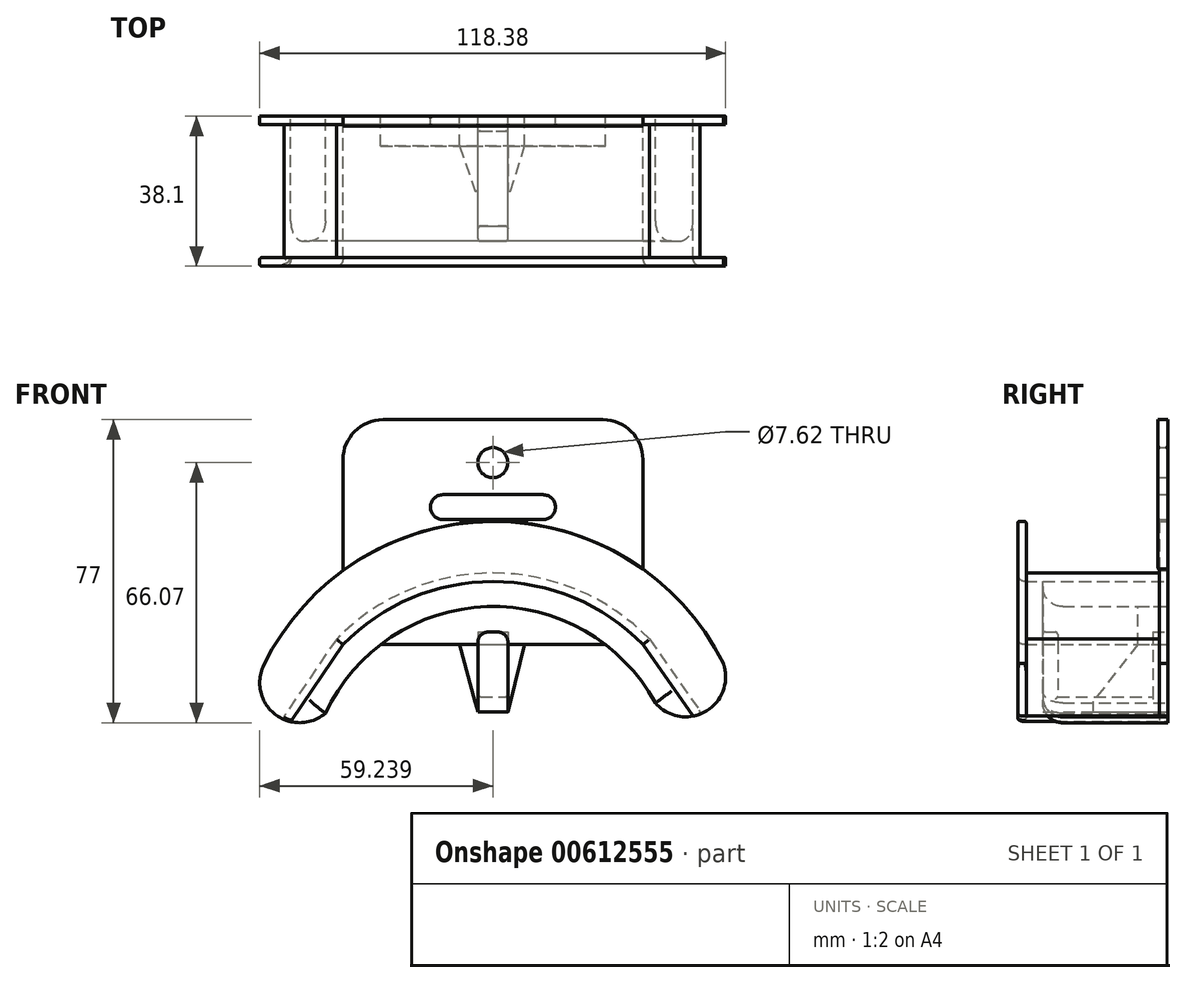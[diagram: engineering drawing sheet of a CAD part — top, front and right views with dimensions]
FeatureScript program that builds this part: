
annotation { "Feature Type Name" : "Feature", "Feature Type Description" : "" }
export const myFeature = defineFeature(function(context is Context, id is Id, definition is map)
    precondition{}
    {
        {
            var Q0;
            Q0=qCreatedBy(makeId("Front.planeOp"),FACE);
            var sketch = newSketch(context, id + "F0", { "sketchPlane" : qUnion([Q0])});
            skLineSegment(sketch, "E0.bottom", {"start": v(-38.1, 57.15) * mm, "end": v(38.1, 57.15) * mm});
            skLineSegment(sketch, "E0.top", {"start": v(-38.1, 0) * mm, "end": v(38.1, 0) * mm});
            skLineSegment(sketch, "E0.left", {"start": v(-38.1, 57.15) * mm, "end": v(-38.1, 0) * mm});
            skLineSegment(sketch, "E0.right", {"start": v(38.1, 57.15) * mm, "end": v(38.1, 0) * mm});
            skArc(sketch, "E1", {"start": v(38.1, 0) * mm, "mid": v(0, 16.02) * mm, "end": v(-38.1, 0) * mm});
            skArc(sketch, "E2.0", {"start": v(41.24, -14.8) * mm, "mid": v(-1.5, 9.64) * mm, "end": v(-42.58, -17.48) * mm});
            skArc(sketch, "E3", {"start": v(-58.24, -5.23) * mm, "mid": v(-55.37, -17.7) * mm, "end": v(-42.58, -17.48) * mm});
            skArc(sketch, "E4", {"start": v(41.24, -14.8) * mm, "mid": v(54.07, -16.97) * mm, "end": v(58.5, -4.73) * mm});
            skLineSegment(sketch, "E5.bottom", {"start": v(-8.48, 0) * mm, "end": v(8.03, 0) * mm});
            skLineSegment(sketch, "E5.right", {"start": v(8.35, 0) * mm, "end": v(8.03, 0) * mm});
            skLineSegment(sketch, "E6", {"start": v(-8.48, 0) * mm, "end": v(-3.83, -17.13) * mm});
            skLineSegment(sketch, "E7", {"start": v(-3.83, -17.13) * mm, "end": v(3.81, -17.13) * mm});
            skLineSegment(sketch, "E8", {"start": v(3.81, -17.13) * mm, "end": v(8.03, 0) * mm});
            skLineSegment(sketch, "E9.bottom", {"start": v(-3.81, 3.2) * mm, "end": v(3.8, 3.2) * mm});
            skLineSegment(sketch, "E9.top", {"start": v(-3.8, -17.13) * mm, "end": v(3.81, -17.13) * mm});
            skLineSegment(sketch, "E9.left", {"start": v(-3.81, 3.2) * mm, "end": v(-3.8, -17.13) * mm});
            skLineSegment(sketch, "E9.right", {"start": v(3.8, 3.2) * mm, "end": v(3.81, -17.13) * mm});
            skLineSegment(sketch, "E10.bottom", {"start": v(-12.7, 38.09) * mm, "end": v(12.7, 38.09) * mm});
            skLineSegment(sketch, "E10.top", {"start": v(-12.7, 31.74) * mm, "end": v(12.7, 31.74) * mm});
            skLineSegment(sketch, "E10.left", {"start": v(-12.7, 38.09) * mm, "end": v(-12.7, 31.74) * mm});
            skLineSegment(sketch, "E10.right", {"start": v(12.7, 38.09) * mm, "end": v(12.7, 31.74) * mm});
            skArc(sketch, "E11", {"start": v(-12.7, 38.09) * mm, "mid": v(-15.88, 34.91) * mm, "end": v(-12.7, 31.74) * mm});
            skArc(sketch, "E12", {"start": v(12.7, 31.74) * mm, "mid": v(15.88, 34.91) * mm, "end": v(12.7, 38.09) * mm});
            skArc(sketch, "E13.0", {"start": v(58.5, -4.73) * mm, "mid": v(-0.03, 31.3) * mm, "end": v(-58.24, -5.23) * mm});
            skLineSegment(sketch, "E14", {"start": v(-38.1, 0) * mm, "end": v(-51.38, -19.6) * mm});
            skLineSegment(sketch, "E15", {"start": v(38.1, 0) * mm, "end": v(50.84, -18.18) * mm});
            skCircle(sketch, "E16", {"center": v(-0.03, 46.22) * mm, "radius": 3.81 * mm});
            skSolve(sketch);
        }
        {
            var Q0;
            {var subQ1=sQuery(id+"F0.wireOp",EDGE,"E0.bottom");Q0=makeQuery(id+"F0.imprint","IMPRINT",FACE,{"disambiguationData":[TD([[makeQuery(id+"F0.imprint","IMPRINT",EDGE,{"derivedFrom":subQ1}),-1.0]])]});}
            extrude(context, id + "F1", {"entities" : qUnion([Q0]), "depth" : 2.54 * mm, "offsetDistance" : 25.4 * mm});
        }
        {
            var Q0;
            {var subQ0=sQuery(id+"F0.wireOp",EDGE,"E1");Q0=makeQuery(id+"F0.imprint","IMPRINT",FACE,{"disambiguationData":[TD([[makeQuery(id+"F0.imprint","IMPRINT",EDGE,{"derivedFrom":subQ0}),1.0]])]});}
            var Q1;
            {var subQ0=sQuery(id+"F0.wireOp",EDGE,"E15");Q1=makeQuery(id+"F0.imprint","IMPRINT",FACE,{"disambiguationData":[TD([[makeQuery(id+"F0.imprint","IMPRINT",EDGE,{"derivedFrom":subQ0}),-1.0]])]});}
            var Q2;
            {var subQ0=sQuery(id+"F0.wireOp",EDGE,"E14");Q2=makeQuery(id+"F0.imprint","IMPRINT",FACE,{"disambiguationData":[TD([[makeQuery(id+"F0.imprint","IMPRINT",EDGE,{"derivedFrom":subQ0}),1.0]])]});}
            extrude(context, id + "F2", {"entities" : qUnion([Q0, Q1, Q2]), "depth" : 31.75 * mm, "offsetDistance" : 25.4 * mm});
        }
        {
            var Q0;
            {var subQ0=sQuery(id+"F0.wireOp",EDGE,"E15");Q0=makeQuery(id+"F0.imprint","IMPRINT",FACE,{"disambiguationData":[TD([[makeQuery(id+"F0.imprint","IMPRINT",EDGE,{"derivedFrom":subQ0}),1.0]])]});}
            var Q1;
            {var subQ0=sQuery(id+"F0.wireOp",EDGE,"E14");Q1=makeQuery(id+"F0.imprint","IMPRINT",FACE,{"disambiguationData":[TD([[makeQuery(id+"F0.imprint","IMPRINT",EDGE,{"derivedFrom":subQ0}),-1.0]])]});}
            var Q2;
            {var subQ0=sQuery(id+"F0.wireOp",EDGE,"E1");Q2=makeQuery(id+"F0.imprint","IMPRINT",FACE,{"disambiguationData":[TD([[makeQuery(id+"F0.imprint","IMPRINT",EDGE,{"derivedFrom":subQ0}),-1.0]])]});}
            var Q3;
            Q3=makeQuery(id+"F2.opExtrude","SWEPT_BODY",BODY,{"disambiguationData":[OSD([sQuery(id+"F0.wireOp",EDGE,"E1"),sQuery(id+"F0.wireOp",EDGE,"E2.0"),sQuery(id+"F0.wireOp",EDGE,"E3"),sQuery(id+"F0.wireOp",EDGE,"E4"),sQuery(id+"F0.wireOp",EDGE,"E14"),sQuery(id+"F0.wireOp",EDGE,"E15")])]});
            var Q4;
            Q4=makeQuery(id+"F2.opExtrude","SWEPT_BODY",BODY,{"disambiguationData":[OSD([sQuery(id+"F0.wireOp",EDGE,"E1"),sQuery(id+"F0.wireOp",EDGE,"E2.0"),sQuery(id+"F0.wireOp",EDGE,"E3"),sQuery(id+"F0.wireOp",EDGE,"E4"),sQuery(id+"F0.wireOp",EDGE,"E14"),sQuery(id+"F0.wireOp",EDGE,"E15")])]});
            extrude(context, id + "F3", {"entities" : qUnion([Q0, Q1, Q2]), "depth" : 38.1 * mm, "endBoundEntityBody" : qUnion([Q3]), "hasOffset" : true, "offsetDistance" : 3.8 * mm, "hasSecondDirectionOffset" : true, "secondDirectionOffsetDistance" : 2.54 * mm});
        }
        {
            var Q0;
            Q0=makeQuery(id+"F3.opExtrude","SWEPT_FACE",FACE,{"disambiguationData":[OSD([sQuery(id+"F0.wireOp",EDGE,"E3")])]});
            var Q1;
            Q1=makeQuery(id+"F3.opExtrude","SWEPT_FACE",FACE,{"disambiguationData":[OSD([sQuery(id+"F0.wireOp",EDGE,"E13.0")])]});
            var Q2;
            Q2=makeQuery(id+"F3.opExtrude","SWEPT_FACE",FACE,{"disambiguationData":[OSD([sQuery(id+"F0.wireOp",EDGE,"E4")])]});
            shell(context, id + "F4", {"entities" : qUnion([Q0, Q1, Q2]), "thickness" : 2.16 * mm});
        }
        {
            var Q0;
            Q0=makeQuery(id+"F1.opExtrude","SWEPT_EDGE",EDGE,{"disambiguationData":[OSD([sQuery(id+"F0.wireOp",EDGE,"E0.bottom"),sQuery(id+"F0.wireOp",EDGE,"E0.left")])]});
            var Q1;
            Q1=makeQuery(id+"F1.opExtrude","SWEPT_EDGE",EDGE,{"disambiguationData":[OSD([sQuery(id+"F0.wireOp",EDGE,"E0.bottom"),sQuery(id+"F0.wireOp",EDGE,"E0.right")])]});
            fillet(context, id + "F5", {"entities" : qUnion([Q0, Q1]), "radius" : 10.16 * mm, "tangentPropagation" : true, "allowEdgeOverflow" : false});
        }
        {
            var Q0;
            {var subQ4=sQuery(id+"F0.wireOp",EDGE,"E9.bottom");Q0=makeQuery(id+"F0.imprint","IMPRINT",FACE,{"disambiguationData":[TD([[makeQuery(id+"F0.imprint","IMPRINT",EDGE,{"derivedFrom":subQ4}),1.0]])]});}
            var Q1;
            {var subQ5=sQuery(id+"F0.wireOp",EDGE,"E9.bottom");Q1=makeQuery(id+"F0.imprint","IMPRINT",FACE,{"disambiguationData":[TD([[makeQuery(id+"F0.imprint","IMPRINT",EDGE,{"derivedFrom":subQ5}),-1.0]])]});}
            extrude(context, id + "F6", {"entities" : qUnion([Q0, Q1]), "depth" : 7.62 * mm, "offsetDistance" : 25.4 * mm});
        }
        {
            var Q0;
            {var subQ5=sQuery(id+"F0.wireOp",EDGE,"E9.bottom");Q0=makeQuery(id+"F0.imprint","IMPRINT",FACE,{"disambiguationData":[TD([[makeQuery(id+"F0.imprint","IMPRINT",EDGE,{"derivedFrom":subQ5}),-1.0]])]});}
            var Q1;
            {var subQ0=sQuery(id+"F0.wireOp",EDGE,"E9.left");var subQ1=sQuery(id+"F0.wireOp",EDGE,"E0.top");var subQ2=makeQuery(id+"F0.imprint","INTERSECT",VERTEX,{"derivedFrom":[subQ1,subQ0]});Q1=makeQuery(id+"F0.imprint","IMPRINT",FACE,{"disambiguationData":[TD([[makeQuery(id+"F0.imprint","IMPRINT",EDGE,{"disambiguationData":[TD([[subQ2,-1.0]])],"derivedFrom":subQ1}),-1.0]])]});}
            extrude(context, id + "F7", {"entities" : qUnion([Q0, Q1]), "depth" : 31.75 * mm, "offsetDistance" : 25.4 * mm});
        }
        {
            var Q0;
            Q0=makeQuery(id+"F7.opExtrude","SWEPT_FACE",FACE,{"disambiguationData":[OSD([sQuery(id+"F0.wireOp",EDGE,"E9.right")])]});
            var Q1;
            Q1=makeQuery(id+"F7.opExtrude","SWEPT_FACE",FACE,{"disambiguationData":[OSD([sQuery(id+"F0.wireOp",EDGE,"E9.bottom")])]});
            var Q2;
            Q2=makeQuery(id+"F7.opExtrude","SWEPT_FACE",FACE,{"disambiguationData":[OSD([sQuery(id+"F0.wireOp",EDGE,"E9.left")])]});
            shell(context, id + "F8", {"entities" : qUnion([Q0, Q1, Q2]), "thickness" : 3.8 * mm});
        }
        {
            var Q0;
            {var subQ0=sQuery(id+"F0.wireOp",EDGE,"E8");Q0=makeQuery(id+"F0.imprint","IMPRINT",FACE,{"disambiguationData":[TD([[makeQuery(id+"F0.imprint","IMPRINT",EDGE,{"derivedFrom":subQ0}),1.0]])]});}
            var Q1;
            {var subQ0=sQuery(id+"F0.wireOp",EDGE,"E6");Q1=makeQuery(id+"F0.imprint","IMPRINT",FACE,{"disambiguationData":[TD([[makeQuery(id+"F0.imprint","IMPRINT",EDGE,{"derivedFrom":subQ0}),1.0]])]});}
            extrude(context, id + "F9", {"entities" : qUnion([Q0, Q1]), "depth" : 19.05 * mm, "offsetDistance" : 25.4 * mm});
        }
        {
            var Q0;
            {var subQ0=sQuery(id+"F0.wireOp",EDGE,"E0.top");Q0=qUnion([makeQuery(id+"F9.opExtrude","CAP_EDGE",EDGE,{"disambiguationData":[OSD([subQ0]),TDD([makeQuery(id+"F0.imprint","IMPRINT",EDGE,{"disambiguationData":[TD([[makeQuery(id+"F0.imprint","INTERSECT",VERTEX,{"derivedFrom":[subQ0,sQuery(id+"F0.wireOp",EDGE,"E6")]}),-1.0]])],"derivedFrom":subQ0})])],"isStart":false}),makeQuery(id+"F9.opExtrude","CAP_EDGE",EDGE,{"disambiguationData":[OSD([subQ0]),TDD([makeQuery(id+"F0.imprint","IMPRINT",EDGE,{"disambiguationData":[TD([[makeQuery(id+"F0.imprint","INTERSECT",VERTEX,{"derivedFrom":[subQ0,sQuery(id+"F0.wireOp",EDGE,"E8")]}),1.0]])],"derivedFrom":subQ0})])],"isStart":false})]);}
            chamfer(context, id + "F10", {"entities" : qUnion([Q0]), "chamferType" : ChamferType.TWO_OFFSETS, "width1" : 11.43 * mm, "oppositeDirection" : false, "width2" : 14.6 * mm, "tangentPropagation" : true});
        }
        {
            var Q0;
            Q0=makeQuery(id+"F7.opExtrude","SWEPT_EDGE",EDGE,{"disambiguationData":[OSD([sQuery(id+"F0.wireOp",EDGE,"E9.bottom"),sQuery(id+"F0.wireOp",EDGE,"E9.right")])]});
            var Q1;
            Q1=makeQuery(id+"F7.opExtrude","SWEPT_EDGE",EDGE,{"disambiguationData":[OSD([sQuery(id+"F0.wireOp",EDGE,"E9.bottom"),sQuery(id+"F0.wireOp",EDGE,"E9.left")])]});
            fillet(context, id + "F11", {"entities" : qUnion([Q0, Q1]), "radius" : 2.54 * mm, "tangentPropagation" : true, "allowEdgeOverflow" : false});
        }
        {
            var Q0;
            {var subQ0=sQuery(id+"F0.wireOp",EDGE,"E9.bottom");Q0=makeQuery(id+"F8.opShell","OFFSET_EDGE",EDGE,{"disambiguationData":[OSD([subQ0]),TDD([makeQuery(id+"F7.opExtrude","CAP_EDGE",EDGE,{"disambiguationData":[OSD([subQ0])],"isStart":false})])]});}
            var Q1;
            Q1=makeQuery(id+"F8.opShell","OFFSET_EDGE",EDGE,{"disambiguationData":[OSD([sQuery(id+"F0.wireOp",EDGE,"E7"),sQuery(id+"F0.wireOp",EDGE,"E8"),sQuery(id+"F0.wireOp",EDGE,"E9.right")])]});
            var Q2;
            Q2=makeQuery(id+"F8.opShell","OFFSET_EDGE",EDGE,{"disambiguationData":[OSD([sQuery(id+"F0.wireOp",EDGE,"E7"),sQuery(id+"F0.wireOp",EDGE,"E9.left")])]});
            var Q3;
            {var subQ0=sQuery(id+"F0.wireOp",EDGE,"E9.right");var subQ1=sQuery(id+"F0.wireOp",EDGE,"E9.bottom");Q3=makeQuery(id+"F11.opFillet","BLEND_EDGE",EDGE,{"blendedFrom":[makeQuery(id+"F7.opExtrude","SWEPT_EDGE",EDGE,{"disambiguationData":[OSD([subQ1,subQ0])]}),makeQuery(id+"F7.opExtrude","CAP_FACE",FACE,{"disambiguationData":[OSD([sQuery(id+"F0.wireOp",EDGE,"E7"),subQ1,sQuery(id+"F0.wireOp",EDGE,"E9.left"),subQ0])],"isStart":false})],"blendedInto":[makeQuery(id+"F7.opExtrude","CAP_FACE",FACE,{"disambiguationData":[OSD([sQuery(id+"F0.wireOp",EDGE,"E7"),subQ1,sQuery(id+"F0.wireOp",EDGE,"E9.left"),subQ0])],"isStart":false})]});}
            fillet(context, id + "F12", {"entities" : qUnion([Q0, Q1, Q2, Q3]), "radius" : 0.64 * mm, "tangentPropagation" : true, "allowEdgeOverflow" : false});
        }
        {
            var Q0;
            Q0=makeQuery(id+"F4.opShell","OFFSET_EDGE",EDGE,{"disambiguationData":[OSD([sQuery(id+"F0.wireOp",EDGE,"E4"),sQuery(id+"F0.wireOp",EDGE,"E15")])]});
            var Q1;
            Q1=makeQuery(id+"F4.opShell","OFFSET_EDGE",EDGE,{"disambiguationData":[OSD([sQuery(id+"F0.wireOp",EDGE,"E3"),sQuery(id+"F0.wireOp",EDGE,"E14")])]});
            fillet(context, id + "F13", {"entities" : qUnion([Q0, Q1]), "radius" : 0.76 * mm, "tangentPropagation" : true, "allowEdgeOverflow" : false});
        }
        {
            var Q0;
            Q0=makeQuery(id+"F3.opExtrude","CAP_EDGE",EDGE,{"disambiguationData":[OSD([sQuery(id+"F0.wireOp",EDGE,"E1")])],"isStart":false});
            var Q1;
            Q1=makeQuery(id+"F3.opExtrude","CAP_EDGE",EDGE,{"disambiguationData":[OSD([sQuery(id+"F0.wireOp",EDGE,"E15")])],"isStart":false});
            var Q2;
            Q2=makeQuery(id+"F3.opExtrude","CAP_EDGE",EDGE,{"disambiguationData":[OSD([sQuery(id+"F0.wireOp",EDGE,"E14")])],"isStart":false});
            fillet(context, id + "F14", {"entities" : qUnion([Q0, Q1, Q2]), "radius" : 1.9 * mm, "tangentPropagation" : true, "allowEdgeOverflow" : false});
        }
        {
            var Q0;
            Q0=makeQuery(id+"F2.opExtrude","CAP_EDGE",EDGE,{"disambiguationData":[OSD([sQuery(id+"F0.wireOp",EDGE,"E2.0")])],"isStart":false});
            var Q1;
            Q1=makeQuery(id+"F2.opExtrude","CAP_EDGE",EDGE,{"disambiguationData":[OSD([sQuery(id+"F0.wireOp",EDGE,"E3")])],"isStart":false});
            var Q2;
            Q2=makeQuery(id+"F2.opExtrude","CAP_EDGE",EDGE,{"disambiguationData":[OSD([sQuery(id+"F0.wireOp",EDGE,"E4")])],"isStart":false});
            fillet(context, id + "F15", {"entities" : qUnion([Q0, Q1, Q2]), "radius" : 5.08 * mm, "tangentPropagation" : true, "allowEdgeOverflow" : false});
        }
        {
            var Q0;
            Q0=makeQuery(id+"F1.opExtrude","CAP_EDGE",EDGE,{"disambiguationData":[OSD([sQuery(id+"F0.wireOp",EDGE,"E10.top")])],"isStart":false});
            var Q1;
            Q1=makeQuery(id+"F1.opExtrude","CAP_EDGE",EDGE,{"disambiguationData":[OSD([sQuery(id+"F0.wireOp",EDGE,"E10.top")])],"isStart":true});
            var Q2;
            Q2=makeQuery(id+"F3.opExtrude","CAP_EDGE",EDGE,{"disambiguationData":[OSD([sQuery(id+"F0.wireOp",EDGE,"E13.0")])],"isStart":false});
            var Q3;
            {var subQ0=sQuery(id+"F0.wireOp",EDGE,"E13.0");Q3=makeQuery(id+"F4.opShell","OFFSET_EDGE",EDGE,{"disambiguationData":[OSD([subQ0]),TDD([makeQuery(id+"F3.opExtrude","CAP_EDGE",EDGE,{"disambiguationData":[OSD([subQ0])],"isStart":false})])]});}
            var Q4;
            Q4=makeQuery(id+"F1.opExtrude","CAP_EDGE",EDGE,{"disambiguationData":[OSD([sQuery(id+"F0.wireOp",EDGE,"E16")])],"isStart":false});
            var Q5;
            Q5=makeQuery(id+"F1.opExtrude","CAP_EDGE",EDGE,{"disambiguationData":[OSD([sQuery(id+"F0.wireOp",EDGE,"E16")])],"isStart":true});
            var Q6;
            Q6=makeQuery(id+"F1.opExtrude","CAP_EDGE",EDGE,{"disambiguationData":[OSD([sQuery(id+"F0.wireOp",EDGE,"E13.0")])],"isStart":false});
            fillet(context, id + "F16", {"entities" : qUnion([Q0, Q1, Q2, Q3, Q4, Q5, Q6]), "radius" : 0.5 * mm, "tangentPropagation" : true, "allowEdgeOverflow" : false});
        }
    });
